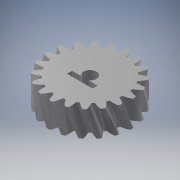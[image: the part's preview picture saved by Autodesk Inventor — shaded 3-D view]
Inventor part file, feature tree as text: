
AUTODESK INVENTOR PART (.ipt)
format: ipt  version: 2017 SP1 (Build 210196100, 196)  size: 438,272 bytes
history: native  units: mm (DEFAULTED — no unit token found)
features: plane x3, other x3, sketch x3, extrude x2
ambient origin geometry x8: Origin, YZ Plane, XZ Plane, XY Plane, X Axis, Y Axis, Z Axis, Center Point
bodies: Solid1 (feature_tree)
feature tree (11):
  extrude  "Extrusion1"  Depth=10.0mm TaperAngle=0.0deg
  plane  "Work Plane2"
  plane  "Work Plane8"
  plane  "Work Plane9"
  other  "Engrenage cylindrique"
  extrude  "Extrusion2"  Depth=10.0mm TaperAngle=0.0deg
  sketch  "Sketch1"  dims[d0=32.749068mm d1=10.0mm d2=0.0mm]
  sketch  "Sketch2"  dims[d3=30.066593mm d4=10.0mm d5=0.0mm d16=30.066593mm d17=0.0mm d34=1.570796mm d39=0.0mm d41=0.0mm d43=30.066593mm d46=30.066593mm d47=0.0mm d48=0.0mm d49=5.0mm d50=10.0mm d51=2.0mm d52=2.0mm d53=5.0mm d54=10.0mm d55=0.0mm]
  other  "Srf1"
  sketch  "Esquisse3"
  other  "Diamètre primitif"
